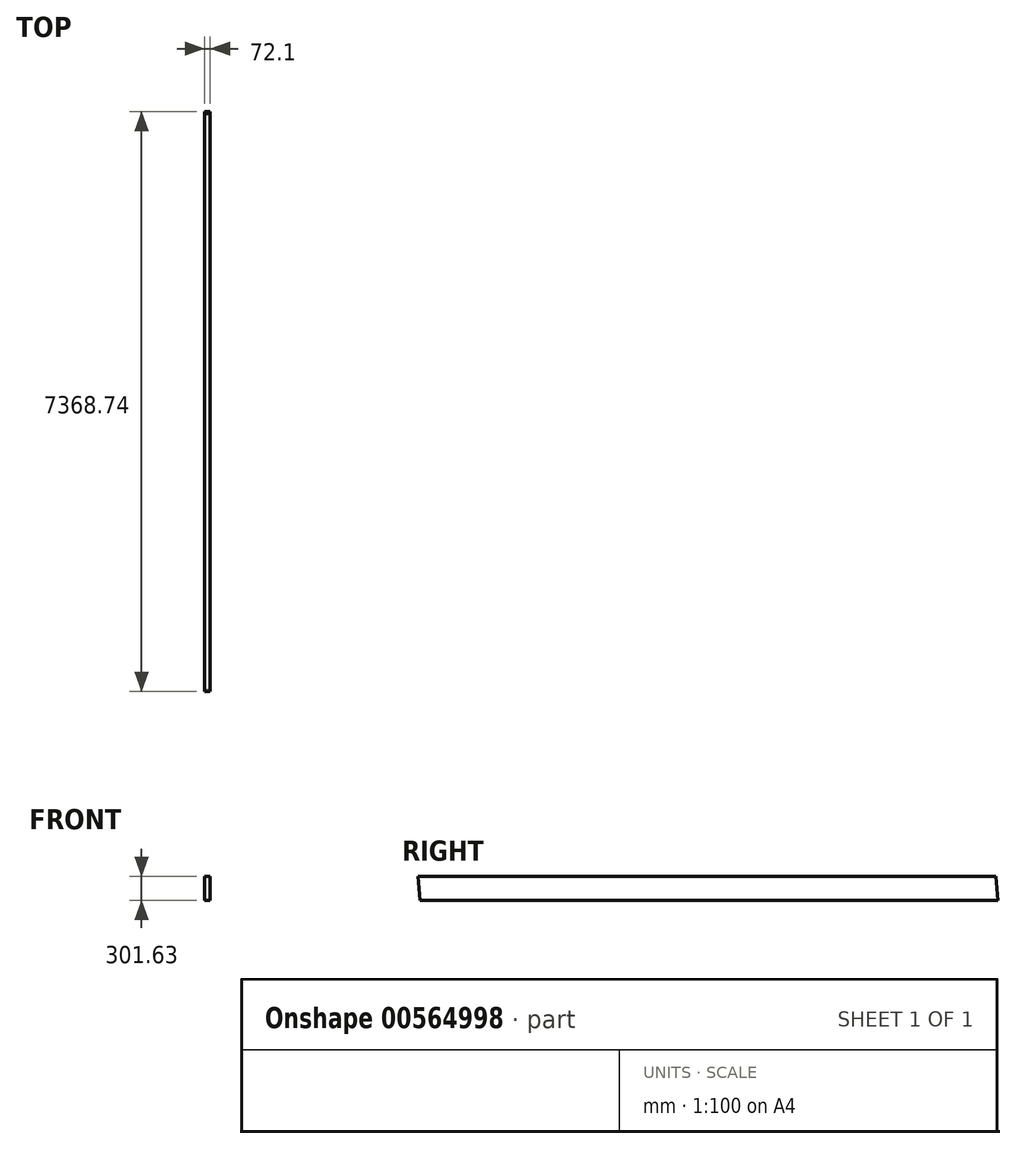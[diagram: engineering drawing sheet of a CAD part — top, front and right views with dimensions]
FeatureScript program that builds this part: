
annotation { "Feature Type Name" : "Feature", "Feature Type Description" : "" }
export const myFeature = defineFeature(function(context is Context, id is Id, definition is map)
    precondition{}
    {
        {
            var Q0;
            Q0=qCreatedBy(makeId("Front.planeOp"),FACE);
            var sketch = newSketch(context, id + "F0", { "sketchPlane" : qUnion([Q0])});
            skLineSegment(sketch, "E0", {"start": v(0, 0) * mm, "end": v(0, 33.65) * mm});
            skLineSegment(sketch, "E1", {"start": v(0, 33.65) * mm, "end": v(31.29, 33.65) * mm});
            skLineSegment(sketch, "E2", {"start": v(31.29, 33.65) * mm, "end": v(31.29, 267.97) * mm});
            skLineSegment(sketch, "E3", {"start": v(31.29, 267.97) * mm, "end": v(0, 267.97) * mm});
            skLineSegment(sketch, "E4", {"start": v(0, 267.97) * mm, "end": v(0, 301.63) * mm});
            skLineSegment(sketch, "E5", {"start": v(0, 301.63) * mm, "end": v(72.1, 301.63) * mm});
            skLineSegment(sketch, "E6", {"start": v(72.1, 301.63) * mm, "end": v(72.1, 267.97) * mm});
            skLineSegment(sketch, "E7", {"start": v(72.1, 267.97) * mm, "end": v(40.81, 267.97) * mm});
            skLineSegment(sketch, "E8", {"start": v(40.81, 267.97) * mm, "end": v(40.81, 33.65) * mm});
            skLineSegment(sketch, "E9", {"start": v(40.81, 33.65) * mm, "end": v(72.1, 33.66) * mm});
            skLineSegment(sketch, "E10", {"start": v(72.1, 33.66) * mm, "end": v(72.1, 0) * mm});
            skLineSegment(sketch, "E11", {"start": v(72.1, 0) * mm, "end": v(0, 0) * mm});
            skSolve(sketch);
        }
        {
            var Q0;
            Q0=qSketchRegion(id+"F0",true);
            extrude(context, id + "F1", {"entities" : qUnion([Q0]), "depth" : 7620 * mm});
        }
        {
            var Q0;
            Q0=makeQuery(id+"F1.opExtrude","SWEPT_FACE",FACE,{"disambiguationData":[OSD([sQuery(id+"F0.wireOp",EDGE,"E10")])]});
            var sketch = newSketch(context, id + "F2", { "sketchPlane" : qUnion([Q0])});
            skLineSegment(sketch, "E12", {"start": v(-140.22, 0) * mm, "end": v(-7149.76, -607.32) * mm, "construction": true});
            skLineSegment(sketch, "E13", {"start": v(-7149.76, -607.32) * mm, "end": v(-7202.38, 0) * mm, "construction": true});
            skLineSegment(sketch, "E14", {"start": v(-7202.38, 0) * mm, "end": v(-7342.6, 0) * mm, "construction": true});
            skLineSegment(sketch, "E15", {"start": v(-7342.6, 0) * mm, "end": v(-7368.74, 301.62) * mm});
            skLineSegment(sketch, "E16", {"start": v(-140.22, 0) * mm, "end": v(0, 0) * mm, "construction": true});
            skLineSegment(sketch, "E17", {"start": v(0, 0) * mm, "end": v(-26.13, 301.63) * mm});
            skLineSegment(sketch, "E18", {"start": v(-26.13, 301.63) * mm, "end": v(-7368.74, 301.62) * mm, "construction": true});
            skLineSegment(sketch, "E19", {"start": v(-7368.74, 301.62) * mm, "end": v(-7620, 301.62) * mm});
            skLineSegment(sketch, "E20", {"start": v(-7620, 301.63) * mm, "end": v(-7620, 0) * mm});
            skLineSegment(sketch, "E21", {"start": v(-7620, 0) * mm, "end": v(-7342.6, 0) * mm});
            skLineSegment(sketch, "E22", {"start": v(0, 0) * mm, "end": v(0, 301.63) * mm});
            skLineSegment(sketch, "E23", {"start": v(0, 301.63) * mm, "end": v(-26.13, 301.63) * mm});
            skSolve(sketch);
        }
        {
            var Q0;
            Q0=qSketchRegion(id+"F2",true);
            extrude(context, id + "F3", {"entities" : qUnion([Q0]), "operationType" : NewBodyOperationType.REMOVE, "endBound" : BoundingType.THROUGH_ALL, "oppositeDirection" : true, "depth" : 25.4 * mm, "offsetDistance" : 25.4 * mm});
        }
        {
            var Q0;
            Q0=makeQuery(id+"F1.opExtrude","SWEPT_FACE",FACE,{"disambiguationData":[OSD([sQuery(id+"F0.wireOp",EDGE,"E8")])]});
            var sketch = newSketch(context, id + "F4", { "sketchPlane" : qUnion([Q0])});
            skLineSegment(sketch, "E24", {"start": v(-7365.82, 267.97) * mm, "end": v(-7345.52, 33.65) * mm});
            skLineSegment(sketch, "E25", {"start": v(-7345.52, 33.65) * mm, "end": v(-2.92, 33.65) * mm});
            skLineSegment(sketch, "E26", {"start": v(-2.92, 33.65) * mm, "end": v(-23.22, 267.97) * mm});
            skLineSegment(sketch, "E27", {"start": v(-23.22, 267.97) * mm, "end": v(-7365.82, 267.97) * mm});
            skSolve(sketch);
        }
        {
            var Q0;
            Q0 = qSketchRegion(id + "F4", true);
            var Q1;
            Q1=makeQuery(id+"F1.opExtrude","SWEPT_FACE",FACE,{"disambiguationData":[OSD([sQuery(id+"F0.wireOp",EDGE,"E6")])]});
            extrude(context, id + "F5", {"entities" : qUnion([Q0]), "operationType" : NewBodyOperationType.ADD, "endBound" : BoundingType.UP_TO_SURFACE, "depth" : 25.4 * mm, "endBoundEntityFace" : qUnion([Q1]), "offsetDistance" : 25.4 * mm});
        }
        {
            var Q0;
            Q0=makeQuery(id+"F1.opExtrude","SWEPT_FACE",FACE,{"disambiguationData":[OSD([sQuery(id+"F0.wireOp",EDGE,"E2")])]});
            var sketch = newSketch(context, id + "F6", { "sketchPlane" : qUnion([Q0])});
            skLineSegment(sketch, "E28", {"start": v(2.92, 33.65) * mm, "end": v(23.22, 267.97) * mm});
            skLineSegment(sketch, "E29", {"start": v(23.22, 267.97) * mm, "end": v(7365.82, 267.97) * mm});
            skLineSegment(sketch, "E30", {"start": v(7365.82, 267.97) * mm, "end": v(7345.52, 33.65) * mm});
            skLineSegment(sketch, "E31", {"start": v(7345.52, 33.65) * mm, "end": v(2.92, 33.65) * mm});
            skSolve(sketch);
        }
        {
            var Q0;
            Q0 = qSketchRegion(id + "F6", true);
            var Q1;
            Q1=makeQuery(id+"F1.opExtrude","SWEPT_FACE",FACE,{"disambiguationData":[OSD([sQuery(id+"F0.wireOp",EDGE,"E4")])]});
            extrude(context, id + "F7", {"entities" : qUnion([Q0]), "operationType" : NewBodyOperationType.ADD, "endBound" : BoundingType.UP_TO_SURFACE, "depth" : 25.4 * mm, "endBoundEntityFace" : qUnion([Q1]), "offsetDistance" : 25.4 * mm});
        }
    });
